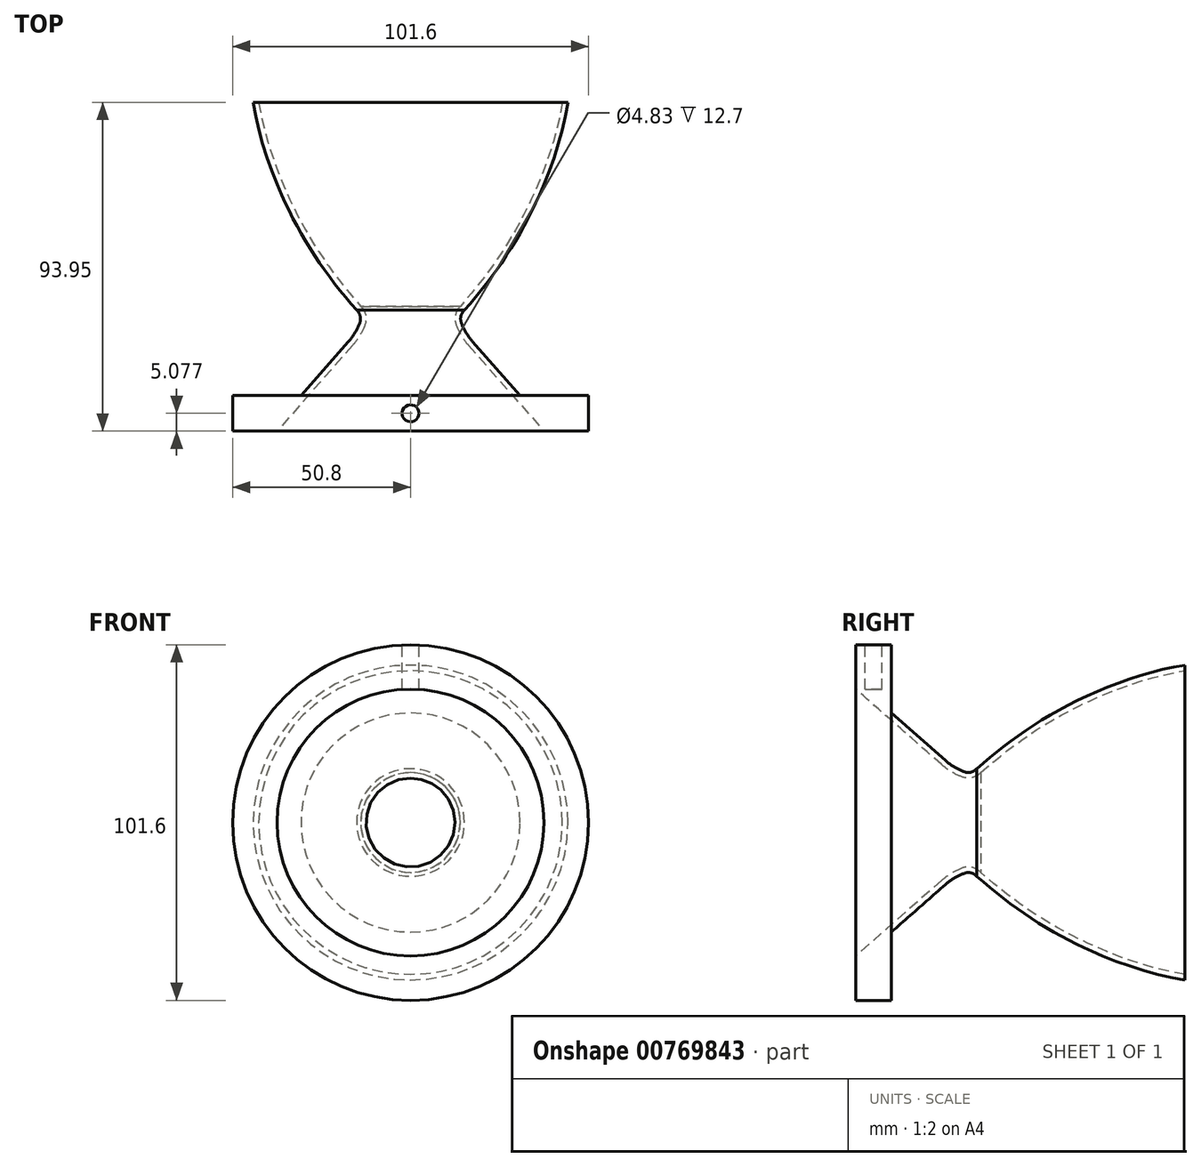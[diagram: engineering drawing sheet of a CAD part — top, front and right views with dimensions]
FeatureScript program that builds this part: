
annotation { "Feature Type Name" : "Feature", "Feature Type Description" : "" }
export const myFeature = defineFeature(function(context is Context, id is Id, definition is map)
    precondition{}
    {
        {
            var Q0;
            Q0=qCreatedBy(makeId("Right.planeOp"),FACE);
            var sketch = newSketch(context, id + "F0", { "sketchPlane" : qUnion([Q0])});
            skPoint(sketch, "E0", {"position": v(0, 12.7) * mm});
            skLineSegment(sketch, "E1", {"start": v(123.7, 0) * mm, "end": v(121.01, 0) * mm});
            skLineSegment(sketch, "E2", {"start": v(-17.44, 25.2) * mm, "end": v(-7.57, 16.53) * mm});
            skArc(sketch, "E3.filletArc", {"start": v(-1.71, 13.01) * mm, "mid": v(1.1, 12.83) * mm, "end": v(3.55, 14.24) * mm});
            skPoint(sketch, "E4.visualSharp", {"position": v(-5.22, 14.47) * mm});
            skArc(sketch, "E4.filletArc", {"start": v(-7.57, 16.53) * mm, "mid": v(-4.8, 14.5) * mm, "end": v(-1.71, 13.01) * mm});
            skPoint(sketch, "E5.visualSharp", {"position": v(-20.49, 27.89) * mm});
            skLineSegment(sketch, "E6", {"start": v(-32.1, 0) * mm, "end": v(0, 0) * mm});
            skFitSpline(sketch, "E7", {"points": [v(3.55, 14.24) * mm, v(34.88, 34.84) * mm, v(80.07, 42.23) * mm, v(104.64, 29.47) * mm], "startDerivative": vector(75.74, 66.28) * mm, "endDerivative": vector(115.64, 5.98) * mm});
            skLineSegment(sketch, "E8", {"start": v(0, -4.1) * mm, "end": v(0, 0) * mm, "construction": true});
            skPoint(sketch, "E9.visualSharp", {"position": v(-17.44, 25.2) * mm});
            skLineSegment(sketch, "E10", {"start": v(61.85, 0) * mm, "end": v(61.85, 43.35) * mm});
            skLineSegment(sketch, "E11.trimOffspring", {"start": v(61.85, 0) * mm, "end": v(0, 0) * mm});
            skLineSegment(sketch, "E12", {"start": v(-32.1, 0) * mm, "end": v(-32.1, 38.1) * mm});
            skLineSegment(sketch, "E13", {"start": v(-17.44, 25.2) * mm, "end": v(-32.1, 38.1) * mm});
            skSolve(sketch);
        }
        {
            var Q0;
            Q0=qSketchRegion(id+"F0",true);
            var Q1;
            Q1=sQuery(id+"F0.wireOp",EDGE,"E1");
            revolve(context, id + "F1", {"entities" : qUnion([Q0]), "axis" : qUnion([Q1]), "revolveType" : RevolveType.FULL});
        }
        {
            var Q0;
            Q0=makeQuery(id+"F1.opRevolve","SWEPT_FACE",FACE,{"disambiguationData":[OSD([sQuery(id+"F0.wireOp",EDGE,"tGUJrLnI-KkJW-VnBt-YyYd-HAQc30k8xeoV")])]});
            var Q1;
            Q1=makeQuery(id+"F1.opRevolve","SWEPT_FACE",FACE,{"disambiguationData":[OSD([sQuery(id+"F0.wireOp",EDGE,"Ow1FXaBQ-uKWU-AUm1-Qf29-WGxy1pBPwJRH")])]});
            var Q2;
            Q2=makeQuery(id+"F1.opRevolve","SWEPT_FACE",FACE,{"disambiguationData":[OSD([sQuery(id+"F0.wireOp",EDGE,"Wp9pB5bN-pT60-1smU-TE8f-r25jIHiwhP3z")])]});
            var Q3;
            Q3=makeQuery(id+"F1.opRevolve","SWEPT_FACE",FACE,{"disambiguationData":[OSD([sQuery(id+"F0.wireOp",EDGE,"kwgIDjig-gaIU-XqJW-MTxW-9zRDGWV0mluJ")])]});
            var Q4;
            Q4=makeQuery(id+"F1.opRevolve","SWEPT_FACE",FACE,{"disambiguationData":[OSD([sQuery(id+"F0.wireOp",EDGE,"E10")])]});
            var Q5;
            Q5=makeQuery(id+"F1.opRevolve","SWEPT_FACE",FACE,{"disambiguationData":[OSD([sQuery(id+"F0.wireOp",EDGE,"E12")])]});
            shell(context, id + "F2", {"entities" : qUnion([Q0, Q1, Q2, Q3, Q4, Q5]), "thickness" : 1.59 * mm, "oppositeDirection" : true});
        }
        {
            var Q0;
            Q0=qCreatedBy(makeId("Right.planeOp"),FACE);
            var sketch = newSketch(context, id + "F3", { "sketchPlane" : qUnion([Q0])});
            skLineSegment(sketch, "E14", {"start": v(-117.34, 0) * mm, "end": v(111.52, 0) * mm, "construction": true});
            skLineSegment(sketch, "E15.1", {"start": v(-6.52, -17.72) * mm, "end": v(-6.52, 17.72) * mm, "construction": true});
            skLineSegment(sketch, "E16", {"start": v(-32.1, -50.8) * mm, "end": v(-21.94, -50.8) * mm});
            skLineSegment(sketch, "E17", {"start": v(-32.1, -38.1) * mm, "end": v(-32.1, -50.8) * mm});
            skLineSegment(sketch, "E18", {"start": v(-6.52, -17.72) * mm, "end": v(-61.38, -65.95) * mm, "construction": true});
            skLineSegment(sketch, "E19", {"start": v(-32.1, -38.1) * mm, "end": v(-21.94, -29.17) * mm});
            skLineSegment(sketch, "E20", {"start": v(-21.94, -29.17) * mm, "end": v(-21.94, -50.8) * mm});
            skSolve(sketch);
        }
        {
            var Q0;
            Q0=makeQuery(id+"F3.imprint","IMPRINT",FACE,{"disambiguationData":[TD([[makeQuery(id+"F3.imprint","IMPRINT",EDGE,{"derivedFrom":sQuery(id+"F3.wireOp",EDGE,"E16")}),1.0]])]});
            var Q1;
            Q1=sQuery(id+"F3.wireOp",EDGE,"E14");
            revolve(context, id + "F4", {"operationType" : NewBodyOperationType.ADD, "surfaceOperationType" : NewSurfaceOperationType.NEW, "entities" : qUnion([Q0]), "axis" : qUnion([Q1]), "revolveType" : RevolveType.FULL});
        }
        {
            var Q0;
            Q0=qCreatedBy(makeId("Top.planeOp"),FACE);
            cPlane(context, id + "F5", {"entities" : qUnion([Q0]), "cplaneType" : CPlaneType.OFFSET, "offset" : 50.8 * mm, "width" : 152.4 * mm, "height" : 152.4 * mm});
        }
        {
            var Q0;
            Q0=qCreatedBy(id+"F5.planeOp",FACE);
            var sketch = newSketch(context, id + "F6", { "sketchPlane" : qUnion([Q0])});
            skCircle(sketch, "E21", {"center": v(0, -27.02) * mm, "radius": 2.41 * mm});
            skSolve(sketch);
        }
        {
            var Q0;
            Q0 = qSketchRegion(id + "F6", true);
            extrude(context, id + "F7", {"entities" : qUnion([Q0]), "operationType" : NewBodyOperationType.REMOVE, "oppositeDirection" : true, "depth" : 12.7 * mm, "offsetDistance" : 25.4 * mm});
        }
    });
